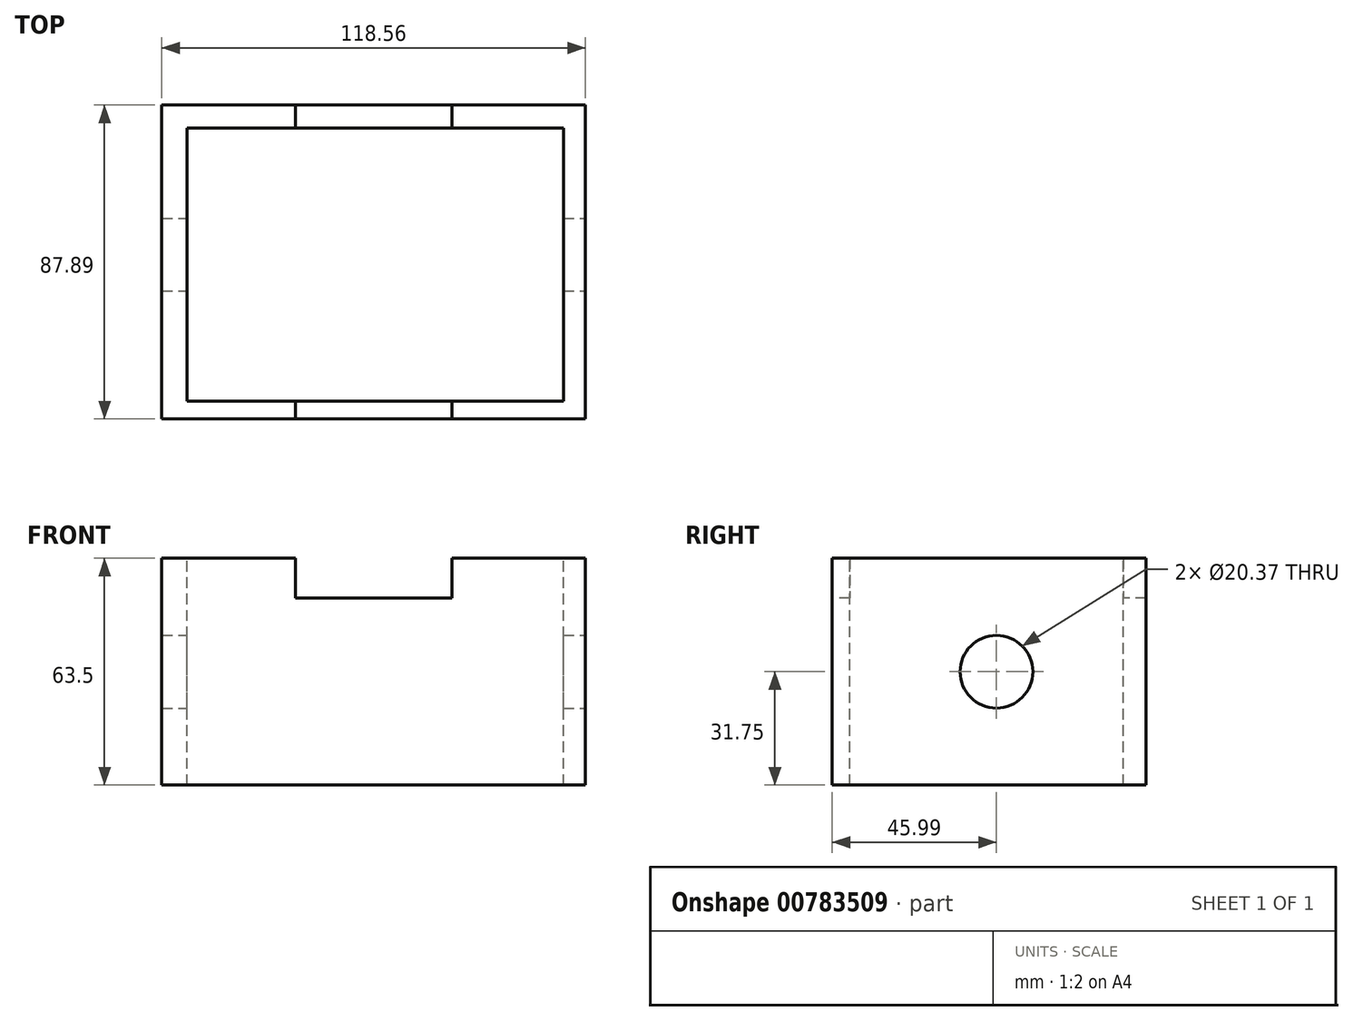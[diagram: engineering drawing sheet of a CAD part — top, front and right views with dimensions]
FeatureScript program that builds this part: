
annotation { "Feature Type Name" : "Feature", "Feature Type Description" : "" }
export const myFeature = defineFeature(function(context is Context, id is Id, definition is map)
    precondition{}
    {
        {
            var Q0;
            Q0=qCreatedBy(makeId("Top.planeOp"),FACE);
            var sketch = newSketch(context, id + "F0", { "sketchPlane" : qUnion([Q0])});
            skLineSegment(sketch, "E0.bottom", {"start": v(-58.84, -46) * mm, "end": v(59.72, -46) * mm});
            skLineSegment(sketch, "E0.top", {"start": v(-58.84, 41.9) * mm, "end": v(59.72, 41.9) * mm});
            skLineSegment(sketch, "E0.left", {"start": v(-58.84, -46) * mm, "end": v(-58.84, 41.9) * mm});
            skLineSegment(sketch, "E0.right", {"start": v(59.72, -46) * mm, "end": v(59.72, 41.9) * mm});
            skSolve(sketch);
        }
        {
            var Q0;
            Q0 = qSketchRegion(id + "F0", true);
            extrude(context, id + "F1", {"entities" : qUnion([Q0]), "depth" : 63.5 * mm, "offsetDistance" : 25.4 * mm});
        }
        {
            var Q0;
            Q0=makeQuery(id+"F1.opExtrude","CAP_FACE",FACE,{"disambiguationData":[OSD([sQuery(id+"F0.wireOp",EDGE,"E0.bottom"),sQuery(id+"F0.wireOp",EDGE,"E0.top"),sQuery(id+"F0.wireOp",EDGE,"E0.left"),sQuery(id+"F0.wireOp",EDGE,"E0.right")])],"isStart":false});
            var sketch = newSketch(context, id + "F2", { "sketchPlane" : qUnion([Q0])});
            skLineSegment(sketch, "E1.bottom", {"start": v(-51.83, -41.03) * mm, "end": v(53.58, -41.03) * mm});
            skLineSegment(sketch, "E1.top", {"start": v(-51.83, 35.48) * mm, "end": v(53.58, 35.48) * mm});
            skLineSegment(sketch, "E1.left", {"start": v(-51.83, -41.03) * mm, "end": v(-51.83, 35.48) * mm});
            skLineSegment(sketch, "E1.right", {"start": v(53.58, -41.03) * mm, "end": v(53.58, 35.48) * mm});
            skSolve(sketch);
        }
        {
            var Q0;
            Q0=makeQuery(id+"F2.imprint","IMPRINT",FACE,{"disambiguationData":[TD([[makeQuery(id+"F2.imprint","IMPRINT",EDGE,{"derivedFrom":sQuery(id+"F2.wireOp",EDGE,"E1.bottom")}),1.0]])]});
            extrude(context, id + "F3", {"entities" : qUnion([Q0]), "operationType" : NewBodyOperationType.REMOVE, "oppositeDirection" : true, "depth" : 63.5 * mm, "offsetDistance" : 25.4 * mm});
        }
        {
            var Q0;
            Q0=makeQuery(id+"F1.opExtrude","SWEPT_FACE",FACE,{"disambiguationData":[OSD([sQuery(id+"F0.wireOp",EDGE,"E0.bottom")])]});
            var sketch = newSketch(context, id + "F4", { "sketchPlane" : qUnion([Q0])});
            skLineSegment(sketch, "E2", {"start": v(-21.46, 63.5) * mm, "end": v(-21.46, 52.42) * mm});
            skLineSegment(sketch, "E3", {"start": v(-21.46, 52.42) * mm, "end": v(0.44, 52.42) * mm});
            skLineSegment(sketch, "E4", {"start": v(0.44, 52.42) * mm, "end": v(22.34, 52.42) * mm});
            skLineSegment(sketch, "E5", {"start": v(22.34, 52.42) * mm, "end": v(22.34, 63.5) * mm});
            skSolve(sketch);
        }
        {
            var Q0;
            {var subQ1=sQuery(id+"F4.wireOp",EDGE,"E2");Q0=makeQuery(id+"F4.imprint","IMPRINT",FACE,{"disambiguationData":[TD([[makeQuery(id+"F4.imprint","IMPRINT",EDGE,{"derivedFrom":subQ1}),1.0]])]});}
            extrude(context, id + "F5", {"entities" : qUnion([Q0]), "operationType" : NewBodyOperationType.REMOVE, "oppositeDirection" : true, "depth" : 127 * mm, "offsetDistance" : 25.4 * mm});
        }
        {
            var Q0;
            Q0=makeQuery(id+"F1.opExtrude","SWEPT_FACE",FACE,{"disambiguationData":[OSD([sQuery(id+"F0.wireOp",EDGE,"E0.right")])]});
            var sketch = newSketch(context, id + "F6", { "sketchPlane" : qUnion([Q0])});
            skCircle(sketch, "E6", {"center": v(0, 31.75) * mm, "radius": 10.18 * mm});
            skPoint(sketch, "E6.centerSnap0", {"position": v(-46, 31.75) * mm});
            skSolve(sketch);
        }
        {
            var Q0;
            Q0=makeQuery(id+"F6.imprint","IMPRINT",FACE,{"disambiguationData":[TD([[makeQuery(id+"F6.imprint","IMPRINT",EDGE,{"derivedFrom":sQuery(id+"F6.wireOp",EDGE,"E6")}),1.0]])]});
            extrude(context, id + "F7", {"entities" : qUnion([Q0]), "operationType" : NewBodyOperationType.REMOVE, "oppositeDirection" : true, "depth" : 254 * mm, "offsetDistance" : 25.4 * mm});
        }
    });
